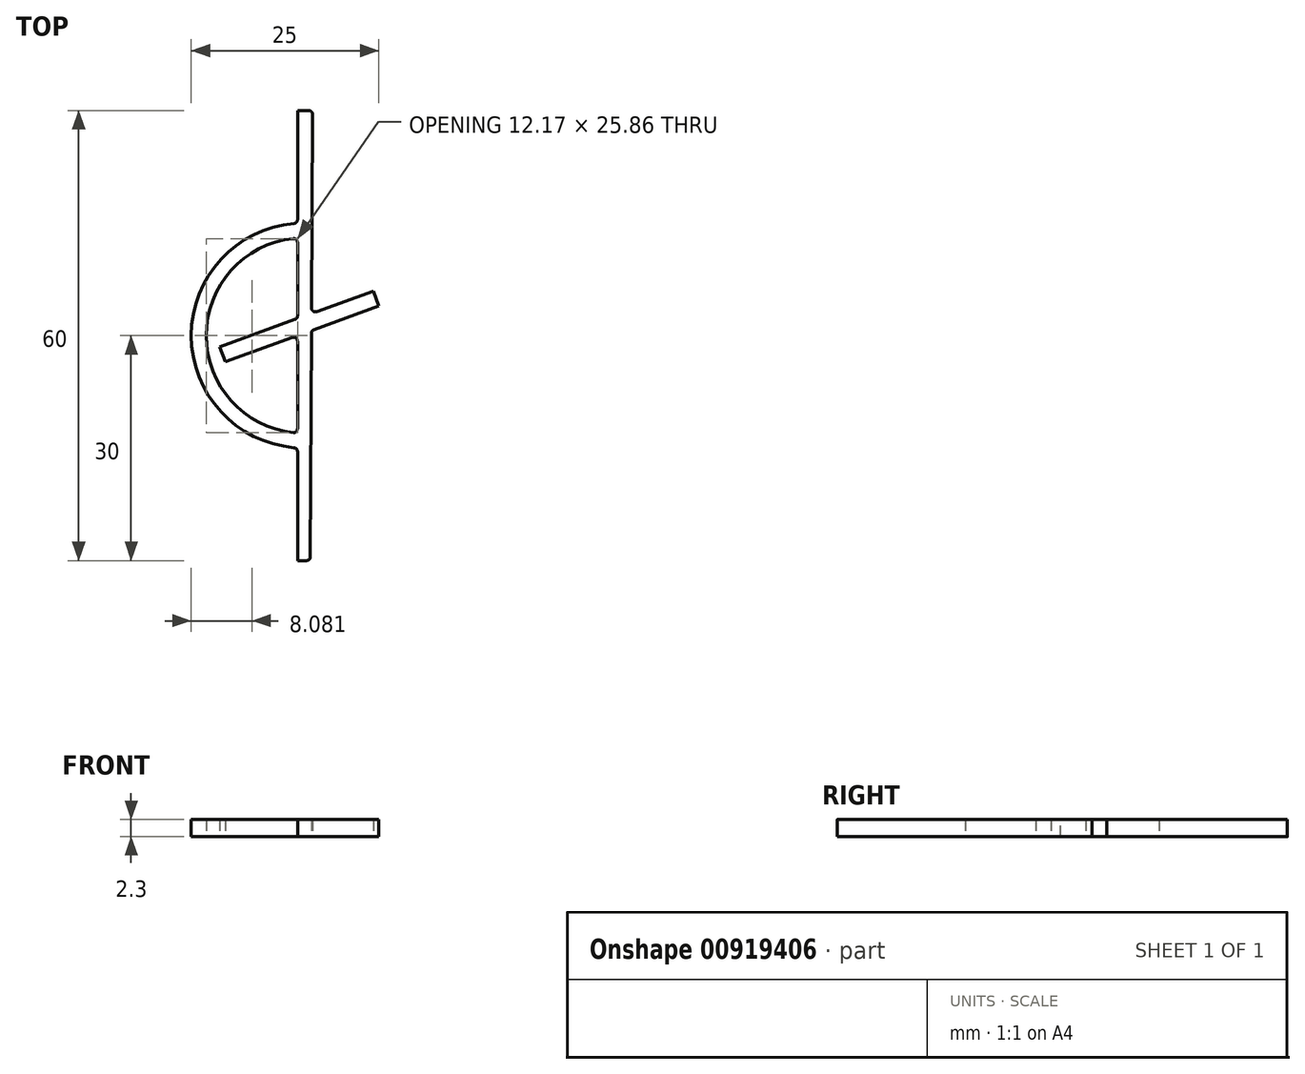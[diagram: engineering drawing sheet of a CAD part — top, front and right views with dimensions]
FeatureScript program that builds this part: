
annotation { "Feature Type Name" : "Feature", "Feature Type Description" : "" }
export const myFeature = defineFeature(function(context is Context, id is Id, definition is map)
    precondition{}
    {
        {
            var Q0;
            Q0=qCreatedBy(makeId("Top.planeOp"),FACE);
            var sketch = newSketch(context, id + "F0", { "sketchPlane" : qUnion([Q0])});
            skLineSegment(sketch, "E0", {"start": v(0, 30) * mm, "end": v(1.17, 30) * mm});
            skLineSegment(sketch, "E1", {"start": v(0, 30) * mm, "end": v(-0.83, 30) * mm});
            skLineSegment(sketch, "E2", {"start": v(-0.83, 30) * mm, "end": v(-0.83, 0) * mm});
            skLineSegment(sketch, "E3", {"start": v(-0.83, 0) * mm, "end": v(-0.83, -30) * mm});
            skLineSegment(sketch, "E4", {"start": v(-0.83, -30) * mm, "end": v(0.87, -30) * mm});
            skLineSegment(sketch, "E5", {"start": v(0.87, -30) * mm, "end": v(1.17, 30) * mm});
            skCircle(sketch, "E6", {"center": v(0, 0) * mm, "radius": 15 * mm});
            skCircle(sketch, "E7", {"center": v(0, 0) * mm, "radius": 13 * mm});
            skLineSegment(sketch, "E8", {"start": v(-10.47, -3.51) * mm, "end": v(-10.37, -3.78) * mm});
            skLineSegment(sketch, "E9", {"start": v(-10.47, -3.51) * mm, "end": v(10, 3.94) * mm});
            skLineSegment(sketch, "E10", {"start": v(-10.37, -3.78) * mm, "end": v(-11.2, -1.51) * mm});
            skLineSegment(sketch, "E11", {"start": v(-11.2, -1.51) * mm, "end": v(9.27, 5.94) * mm});
            skLineSegment(sketch, "E12", {"start": v(10, 3.94) * mm, "end": v(9.27, 5.94) * mm});
            skSolve(sketch);
        }
        {
            var Q0;
            {var subQ0=sQuery(id+"F0.wireOp",EDGE,"E7");var subQ1=sQuery(id+"F0.wireOp",EDGE,"E2");var subQ2=makeQuery(id+"F0.imprint","INTERSECT",VERTEX,{"derivedFrom":[subQ1,subQ0]});Q0=makeQuery(id+"F0.imprint","IMPRINT",FACE,{"disambiguationData":[TD([[makeQuery(id+"F0.imprint","IMPRINT",EDGE,{"disambiguationData":[TD([[subQ2,-1.0]])],"derivedFrom":subQ1}),1.0]])]});}
            var Q1;
            {var subQ0=sQuery(id+"F0.wireOp",EDGE,"E6");var subQ1=sQuery(id+"F0.wireOp",EDGE,"E2");var subQ2=makeQuery(id+"F0.imprint","INTERSECT",VERTEX,{"derivedFrom":[subQ1,subQ0]});Q1=makeQuery(id+"F0.imprint","IMPRINT",FACE,{"disambiguationData":[TD([[makeQuery(id+"F0.imprint","IMPRINT",EDGE,{"disambiguationData":[TD([[subQ2,-1.0]])],"derivedFrom":subQ1}),1.0]])]});}
            var Q2;
            {var subQ1=sQuery(id+"F0.wireOp",EDGE,"E0");Q2=makeQuery(id+"F0.imprint","IMPRINT",FACE,{"disambiguationData":[TD([[makeQuery(id+"F0.imprint","IMPRINT",EDGE,{"derivedFrom":subQ1}),-1.0]])]});}
            var Q3;
            {var subQ0=sQuery(id+"F0.wireOp",EDGE,"E6");var subQ1=sQuery(id+"F0.wireOp",EDGE,"E5");var subQ2=makeQuery(id+"F0.imprint","INTERSECT",VERTEX,{"disambiguationData":[OD(0.0)],"derivedFrom":[subQ1,subQ0]});Q3=makeQuery(id+"F0.imprint","IMPRINT",FACE,{"disambiguationData":[TD([[makeQuery(id+"F0.imprint","IMPRINT",EDGE,{"disambiguationData":[TD([[subQ2,-1.0]])],"derivedFrom":subQ1}),-1.0]])]});}
            var Q4;
            {var subQ0=sQuery(id+"F0.wireOp",EDGE,"E6");var subQ1=sQuery(id+"F0.wireOp",EDGE,"E2");var subQ2=makeQuery(id+"F0.imprint","INTERSECT",VERTEX,{"derivedFrom":[subQ1,subQ0]});Q4=makeQuery(id+"F0.imprint","IMPRINT",FACE,{"disambiguationData":[TD([[makeQuery(id+"F0.imprint","IMPRINT",EDGE,{"disambiguationData":[TD([[subQ2,-1.0]])],"derivedFrom":subQ1}),-1.0]])]});}
            var Q5;
            {var subQ5=sQuery(id+"F0.wireOp",EDGE,"E3");var subQ7=sQuery(id+"F0.wireOp",EDGE,"E2");var subQ8=makeQuery(id+"F0.imprint","INTERSECT",VERTEX,{"derivedFrom":[subQ7,subQ5]});Q5=makeQuery(id+"F0.imprint","IMPRINT",FACE,{"disambiguationData":[TD([[makeQuery(id+"F0.imprint","IMPRINT",EDGE,{"disambiguationData":[TD([[subQ8,1.0]])],"derivedFrom":subQ7}),-1.0]])]});}
            var Q6;
            {var subQ5=sQuery(id+"F0.wireOp",EDGE,"E12");Q6=makeQuery(id+"F0.imprint","IMPRINT",FACE,{"disambiguationData":[TD([[makeQuery(id+"F0.imprint","IMPRINT",EDGE,{"derivedFrom":subQ5}),1.0]])]});}
            var Q7;
            {var subQ1=sQuery(id+"F0.wireOp",EDGE,"E3");var subQ5=sQuery(id+"F0.wireOp",EDGE,"E2");var subQ6=makeQuery(id+"F0.imprint","INTERSECT",VERTEX,{"derivedFrom":[subQ5,subQ1]});Q7=makeQuery(id+"F0.imprint","IMPRINT",FACE,{"disambiguationData":[TD([[makeQuery(id+"F0.imprint","IMPRINT",EDGE,{"disambiguationData":[TD([[subQ6,1.0]])],"derivedFrom":subQ5}),1.0]])]});}
            var Q8;
            {var subQ0=sQuery(id+"F0.wireOp",EDGE,"E9");var subQ1=sQuery(id+"F0.wireOp",EDGE,"E3");var subQ2=makeQuery(id+"F0.imprint","INTERSECT",VERTEX,{"derivedFrom":[subQ1,subQ0]});Q8=makeQuery(id+"F0.imprint","IMPRINT",FACE,{"disambiguationData":[TD([[makeQuery(id+"F0.imprint","IMPRINT",EDGE,{"disambiguationData":[TD([[subQ2,-1.0]])],"derivedFrom":subQ1}),1.0]])]});}
            var Q9;
            {var subQ0=sQuery(id+"F0.wireOp",EDGE,"E6");var subQ1=sQuery(id+"F0.wireOp",EDGE,"E3");var subQ2=makeQuery(id+"F0.imprint","INTERSECT",VERTEX,{"derivedFrom":[subQ1,subQ0]});Q9=makeQuery(id+"F0.imprint","IMPRINT",FACE,{"disambiguationData":[TD([[makeQuery(id+"F0.imprint","IMPRINT",EDGE,{"disambiguationData":[TD([[subQ2,1.0]])],"derivedFrom":subQ1}),1.0]])]});}
            var Q10;
            {var subQ0=sQuery(id+"F0.wireOp",EDGE,"E4");Q10=makeQuery(id+"F0.imprint","IMPRINT",FACE,{"disambiguationData":[TD([[makeQuery(id+"F0.imprint","IMPRINT",EDGE,{"derivedFrom":subQ0}),1.0]])]});}
            extrude(context, id + "F1", {"entities" : qUnion([Q0, Q1, Q2, Q3, Q4, Q5, Q6, Q7, Q8, Q9, Q10]), "depth" : 2.3 * mm, "offsetDistance" : 25.4 * mm});
        }
        {
            var Q0;
            Q0=makeQuery(id+"F1.opExtrude","SWEPT_EDGE",EDGE,{"disambiguationData":[OSD([sQuery(id+"F0.wireOp",EDGE,"E2"),sQuery(id+"F0.wireOp",EDGE,"E6")])]});
            var Q1;
            {var subQ0=sQuery(id+"F0.wireOp",EDGE,"E6");var subQ1=sQuery(id+"F0.wireOp",EDGE,"E5");Q1=makeQuery(id+"F1.opExtrude","SWEPT_EDGE",EDGE,{"disambiguationData":[OSD([subQ1,subQ0]),TDD([makeQuery(id+"F0.imprint","INTERSECT",VERTEX,{"disambiguationData":[OD(1.0)],"derivedFrom":[subQ1,subQ0]})])]});}
            var Q2;
            Q2=makeQuery(id+"F1.opExtrude","SWEPT_EDGE",EDGE,{"disambiguationData":[OSD([sQuery(id+"F0.wireOp",EDGE,"E5"),sQuery(id+"F0.wireOp",EDGE,"E11")])]});
            var Q3;
            {var subQ0=sQuery(id+"F0.wireOp",EDGE,"E7");var subQ1=sQuery(id+"F0.wireOp",EDGE,"E5");Q3=makeQuery(id+"F1.opExtrude","SWEPT_EDGE",EDGE,{"disambiguationData":[OSD([subQ1,subQ0]),TDD([makeQuery(id+"F0.imprint","INTERSECT",VERTEX,{"disambiguationData":[OD(0.0)],"derivedFrom":[subQ1,subQ0]})])]});}
            var Q4;
            Q4=makeQuery(id+"F1.opExtrude","SWEPT_EDGE",EDGE,{"disambiguationData":[OSD([sQuery(id+"F0.wireOp",EDGE,"E2"),sQuery(id+"F0.wireOp",EDGE,"E11")])]});
            var Q5;
            Q5=makeQuery(id+"F1.opExtrude","SWEPT_EDGE",EDGE,{"disambiguationData":[OSD([sQuery(id+"F0.wireOp",EDGE,"E3"),sQuery(id+"F0.wireOp",EDGE,"E7")])]});
            var Q6;
            Q6=makeQuery(id+"F1.opExtrude","SWEPT_EDGE",EDGE,{"disambiguationData":[OSD([sQuery(id+"F0.wireOp",EDGE,"E2"),sQuery(id+"F0.wireOp",EDGE,"E7")])]});
            var Q7;
            Q7=makeQuery(id+"F1.opExtrude","SWEPT_EDGE",EDGE,{"disambiguationData":[OSD([sQuery(id+"F0.wireOp",EDGE,"E3"),sQuery(id+"F0.wireOp",EDGE,"E9")])]});
            var Q8;
            Q8=makeQuery(id+"F1.opExtrude","SWEPT_EDGE",EDGE,{"disambiguationData":[OSD([sQuery(id+"F0.wireOp",EDGE,"E3"),sQuery(id+"F0.wireOp",EDGE,"E6")])]});
            var Q9;
            {var subQ0=sQuery(id+"F0.wireOp",EDGE,"E6");var subQ1=sQuery(id+"F0.wireOp",EDGE,"E5");Q9=makeQuery(id+"F1.opExtrude","SWEPT_EDGE",EDGE,{"disambiguationData":[OSD([subQ1,subQ0]),TDD([makeQuery(id+"F0.imprint","INTERSECT",VERTEX,{"disambiguationData":[OD(0.0)],"derivedFrom":[subQ1,subQ0]})])]});}
            var Q10;
            {var subQ0=sQuery(id+"F0.wireOp",EDGE,"E7");var subQ1=sQuery(id+"F0.wireOp",EDGE,"E5");Q10=makeQuery(id+"F1.opExtrude","SWEPT_EDGE",EDGE,{"disambiguationData":[OSD([subQ1,subQ0]),TDD([makeQuery(id+"F0.imprint","INTERSECT",VERTEX,{"disambiguationData":[OD(1.0)],"derivedFrom":[subQ1,subQ0]})])]});}
            var Q11;
            Q11=makeQuery(id+"F1.opExtrude","SWEPT_EDGE",EDGE,{"disambiguationData":[OSD([sQuery(id+"F0.wireOp",EDGE,"E5"),sQuery(id+"F0.wireOp",EDGE,"E9")])]});
            fillet(context, id + "F2", {"entities" : qUnion([Q0, Q1, Q2, Q3, Q4, Q5, Q6, Q7, Q8, Q9, Q10, Q11]), "radius" : 0.5 * mm, "tangentPropagation" : true, "allowEdgeOverflow" : false});
        }
    });
